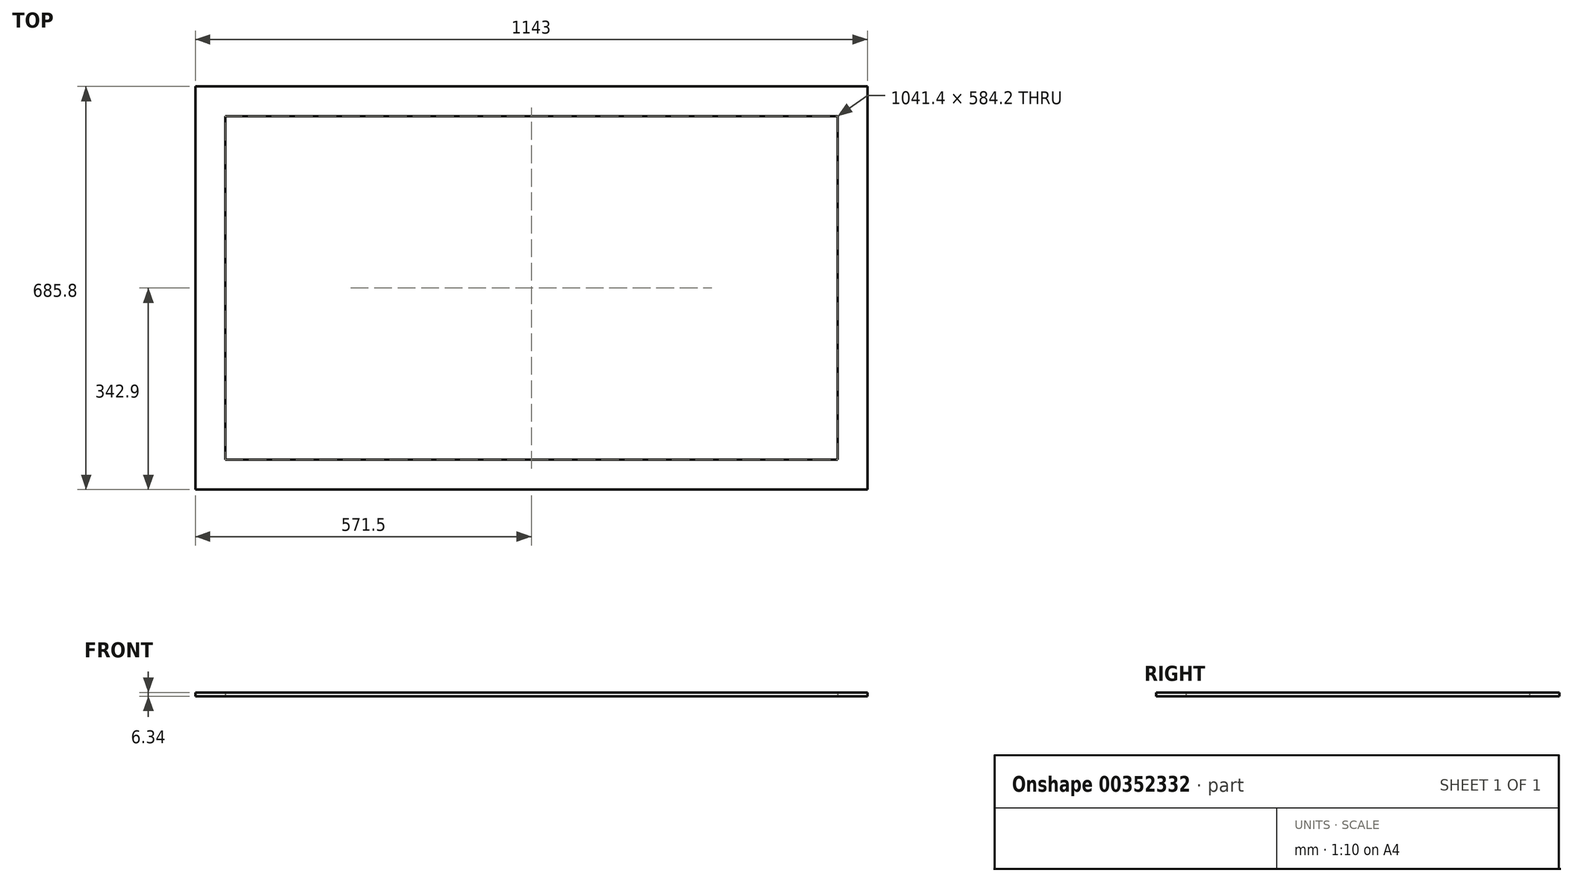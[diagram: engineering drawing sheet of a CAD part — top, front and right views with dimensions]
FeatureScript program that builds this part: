
annotation { "Feature Type Name" : "Feature", "Feature Type Description" : "" }
export const myFeature = defineFeature(function(context is Context, id is Id, definition is map)
    precondition{}
    {
        {
            var Q0;
            Q0=qCreatedBy(makeId("Top.planeOp"),FACE);
            var sketch = newSketch(context, id + "F0", { "sketchPlane" : qUnion([Q0])});
            skPoint(sketch, "E0.middle", {"position": v(0, 0) * mm});
            skLineSegment(sketch, "E1.0", {"start": v(520.7, 292.1) * mm, "end": v(-520.7, 292.1) * mm});
            skLineSegment(sketch, "E1.1", {"start": v(520.7, 292.1) * mm, "end": v(520.7, -292.1) * mm});
            skLineSegment(sketch, "E1.2", {"start": v(520.7, -292.1) * mm, "end": v(-520.7, -292.1) * mm});
            skLineSegment(sketch, "E1.3", {"start": v(-520.7, 292.1) * mm, "end": v(-520.7, -292.1) * mm});
            skLineSegment(sketch, "E2.0", {"start": v(571.5, 342.9) * mm, "end": v(-571.5, 342.9) * mm});
            skLineSegment(sketch, "E2.1", {"start": v(571.5, 342.9) * mm, "end": v(571.5, -342.9) * mm});
            skLineSegment(sketch, "E2.2", {"start": v(571.5, -342.9) * mm, "end": v(-571.5, -342.9) * mm});
            skLineSegment(sketch, "E2.3", {"start": v(-571.5, 342.9) * mm, "end": v(-571.5, -342.9) * mm});
            skSolve(sketch);
        }
        {
            var Q0;
            Q0 = qSketchRegion(id + "F0", true);
            extrude(context, id + "F1", {"entities" : qUnion([Q0]), "endBound" : BoundingType.SYMMETRIC, "depth" : 6.35 * mm});
        }
    });
